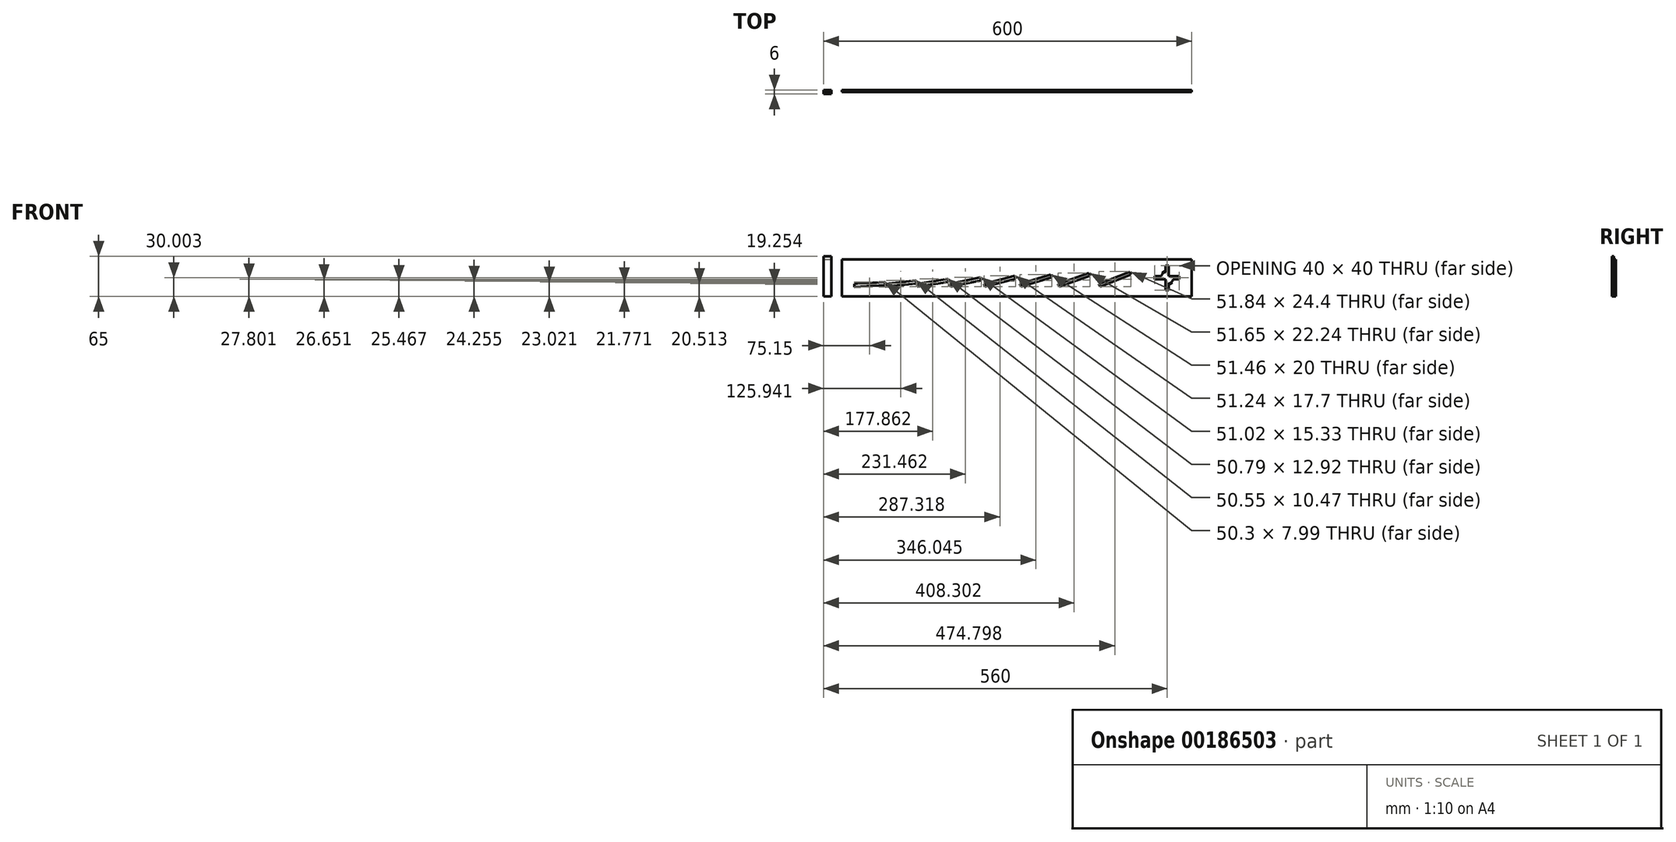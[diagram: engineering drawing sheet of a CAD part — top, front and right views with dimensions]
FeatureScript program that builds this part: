
annotation { "Feature Type Name" : "Feature", "Feature Type Description" : "" }
export const myFeature = defineFeature(function(context is Context, id is Id, definition is map)
    precondition{}
    {
        {
            var Q0;
            Q0=qCreatedBy(makeId("Front.planeOp"),FACE);
            var sketch = newSketch(context, id + "F0", { "sketchPlane" : qUnion([Q0])});
            skLineSegment(sketch, "E0", {"start": v(0, 0) * mm, "end": v(600, 0) * mm, "construction": true});
            skLineSegment(sketch, "E1", {"start": v(0, 0) * mm, "end": v(0, 500) * mm, "construction": true});
            skCircle(sketch, "E2", {"center": v(0, 500) * mm, "radius": 25 * mm, "construction": true});
            skLineSegment(sketch, "E3", {"start": v(0, 500) * mm, "end": v(25, 500) * mm, "construction": true});
            skLineSegment(sketch, "E4", {"start": v(25, 500) * mm, "end": v(600, 500) * mm, "construction": true});
            skLineSegment(sketch, "E5", {"start": v(35, 500) * mm, "end": v(35, 0) * mm, "construction": true});
            skLineSegment(sketch, "E6", {"start": v(35, 0) * mm, "end": v(-24.82, 497.01) * mm, "construction": true});
            skLineSegment(sketch, "E7", {"start": v(85.36, 0) * mm, "end": v(85.36, 3.02) * mm, "construction": true});
            skLineSegment(sketch, "E8", {"start": v(85.36, 0) * mm, "end": v(85, 3) * mm, "construction": true});
            skLineSegment(sketch, "E9", {"start": v(35, 0) * mm, "end": v(85, 3) * mm});
            skLineSegment(sketch, "E10", {"start": v(85, 3) * mm, "end": v(24.82, 502.99) * mm, "construction": true});
            skLineSegment(sketch, "E11", {"start": v(85, 3) * mm, "end": v(85, 3) * mm});
            skLineSegment(sketch, "E12", {"start": v(85, 3) * mm, "end": v(85.36, 3.02) * mm, "construction": true});
            skLineSegment(sketch, "E13", {"start": v(85.67, 0) * mm, "end": v(-24.4, 494.57) * mm, "construction": true});
            skLineSegment(sketch, "E14", {"start": v(136.9, 0) * mm, "end": v(135.67, 5.5) * mm, "construction": true});
            skLineSegment(sketch, "E15", {"start": v(136.9, 0) * mm, "end": v(136.9, 5.63) * mm, "construction": true});
            skLineSegment(sketch, "E16", {"start": v(85.67, 0) * mm, "end": v(135.67, 5.5) * mm});
            skLineSegment(sketch, "E17", {"start": v(135.67, 5.5) * mm, "end": v(24.14, 506.62) * mm, "construction": true});
            skLineSegment(sketch, "E18", {"start": v(135.67, 5.5) * mm, "end": v(136.9, 5.63) * mm, "construction": true});
            skLineSegment(sketch, "E19", {"start": v(137.47, 0) * mm, "end": v(-23.76, 492.22) * mm, "construction": true});
            skLineSegment(sketch, "E20", {"start": v(190.08, 0) * mm, "end": v(190.08, 8.4) * mm, "construction": true});
            skLineSegment(sketch, "E21", {"start": v(137.47, 0) * mm, "end": v(187.47, 7.98) * mm});
            skLineSegment(sketch, "E22", {"start": v(190.08, 0) * mm, "end": v(187.47, 7.98) * mm, "construction": true});
            skLineSegment(sketch, "E23", {"start": v(187.47, 7.98) * mm, "end": v(23.76, 507.78) * mm, "construction": true});
            skLineSegment(sketch, "E24", {"start": v(187.47, 7.98) * mm, "end": v(190.08, 8.4) * mm, "construction": true});
            skLineSegment(sketch, "E25", {"start": v(190.95, 0) * mm, "end": v(-22.91, 490) * mm, "construction": true});
            skLineSegment(sketch, "E26", {"start": v(245.5, 0) * mm, "end": v(240.95, 10.44) * mm, "construction": true});
            skLineSegment(sketch, "E27", {"start": v(245.5, 0) * mm, "end": v(245.5, 11.39) * mm, "construction": true});
            skLineSegment(sketch, "E28", {"start": v(190.95, 0) * mm, "end": v(240.95, 10.44) * mm});
            skLineSegment(sketch, "E29", {"start": v(240.95, 10.44) * mm, "end": v(22.91, 510) * mm, "construction": true});
            skLineSegment(sketch, "E30", {"start": v(240.95, 10.44) * mm, "end": v(245.5, 11.39) * mm, "construction": true});
            skLineSegment(sketch, "E31", {"start": v(246.7, 0) * mm, "end": v(-21.9, 487.94) * mm, "construction": true});
            skLineSegment(sketch, "E32", {"start": v(303.77, 0) * mm, "end": v(303.77, 14.67) * mm, "construction": true});
            skLineSegment(sketch, "E33", {"start": v(246.7, 0) * mm, "end": v(296.7, 12.85) * mm});
            skLineSegment(sketch, "E34", {"start": v(303.77, 0) * mm, "end": v(296.7, 12.85) * mm, "construction": true});
            skLineSegment(sketch, "E35", {"start": v(296.7, 12.85) * mm, "end": v(21.9, 512.06) * mm, "construction": true});
            skLineSegment(sketch, "E36", {"start": v(296.7, 12.85) * mm, "end": v(303.77, 14.67) * mm, "construction": true});
            skLineSegment(sketch, "E37", {"start": v(305.32, 0) * mm, "end": v(-20.76, 486.07) * mm, "construction": true});
            skLineSegment(sketch, "E38", {"start": v(365.53, 0) * mm, "end": v(365.53, 18.32) * mm, "construction": true});
            skLineSegment(sketch, "E39", {"start": v(305.32, 0) * mm, "end": v(355.32, 15.22) * mm});
            skLineSegment(sketch, "E40", {"start": v(365.53, 0) * mm, "end": v(355.32, 15.22) * mm, "construction": true});
            skLineSegment(sketch, "E41", {"start": v(355.32, 15.22) * mm, "end": v(20.76, 513.93) * mm, "construction": true});
            skLineSegment(sketch, "E42", {"start": v(355.32, 15.22) * mm, "end": v(365.53, 18.32) * mm, "construction": true});
            skLineSegment(sketch, "E43", {"start": v(431.47, 0) * mm, "end": v(431.47, 22.43) * mm, "construction": true});
            skLineSegment(sketch, "E44", {"start": v(367.48, 0) * mm, "end": v(-19.53, 484.4) * mm, "construction": true});
            skLineSegment(sketch, "E45", {"start": v(431.47, 0) * mm, "end": v(417.48, 17.52) * mm, "construction": true});
            skLineSegment(sketch, "E46", {"start": v(367.48, 0) * mm, "end": v(417.48, 17.52) * mm});
            skLineSegment(sketch, "E47", {"start": v(417.48, 17.52) * mm, "end": v(19.53, 515.6) * mm, "construction": true});
            skLineSegment(sketch, "E48", {"start": v(417.48, 17.52) * mm, "end": v(431.47, 22.43) * mm, "construction": true});
            skLineSegment(sketch, "E49", {"start": v(433.88, 0) * mm, "end": v(-18.25, 482.91) * mm, "construction": true});
            skLineSegment(sketch, "E50", {"start": v(502.37, 0) * mm, "end": v(502.37, 27.06) * mm, "construction": true});
            skLineSegment(sketch, "E51", {"start": v(502.37, 0) * mm, "end": v(483.88, 19.75) * mm, "construction": true});
            skLineSegment(sketch, "E52", {"start": v(433.88, 0) * mm, "end": v(483.88, 19.75) * mm});
            skLineSegment(sketch, "E53", {"start": v(483.88, 19.75) * mm, "end": v(18.25, 517.09) * mm, "construction": true});
            skLineSegment(sketch, "E54", {"start": v(483.88, 19.75) * mm, "end": v(502.37, 27.06) * mm, "construction": true});
            skLineSegment(sketch, "E55.bottom", {"start": v(-15, -20.25) * mm, "end": v(585, -20.25) * mm});
            skLineSegment(sketch, "E55.top", {"start": v(-15, 39.75) * mm, "end": v(585, 39.75) * mm});
            skLineSegment(sketch, "E55.left", {"start": v(-15, -20.25) * mm, "end": v(-15, 39.75) * mm});
            skLineSegment(sketch, "E55.right", {"start": v(585, -20.25) * mm, "end": v(585, 39.75) * mm});
            skLineSegment(sketch, "E56", {"start": v(35, 0) * mm, "end": v(35.3, -5) * mm});
            skLineSegment(sketch, "E57", {"start": v(35.3, -5) * mm, "end": v(85.3, -2) * mm});
            skLineSegment(sketch, "E58", {"start": v(85, 3) * mm, "end": v(85.3, -2) * mm});
            skLineSegment(sketch, "E59", {"start": v(85.67, 0) * mm, "end": v(86.21, -4.97) * mm});
            skLineSegment(sketch, "E60", {"start": v(86.21, -4.97) * mm, "end": v(136.21, 0.53) * mm});
            skLineSegment(sketch, "E61", {"start": v(135.67, 5.5) * mm, "end": v(136.21, 0.53) * mm});
            skLineSegment(sketch, "E62", {"start": v(137.47, 0) * mm, "end": v(138.26, -4.94) * mm});
            skLineSegment(sketch, "E63", {"start": v(138.26, -4.94) * mm, "end": v(188.26, 3.04) * mm});
            skLineSegment(sketch, "E64", {"start": v(187.47, 7.98) * mm, "end": v(188.26, 3.04) * mm});
            skLineSegment(sketch, "E65", {"start": v(190.95, 0) * mm, "end": v(191.97, -4.9) * mm});
            skLineSegment(sketch, "E66", {"start": v(191.97, -4.9) * mm, "end": v(241.97, 5.54) * mm});
            skLineSegment(sketch, "E67", {"start": v(240.95, 10.44) * mm, "end": v(241.97, 5.54) * mm});
            skLineSegment(sketch, "E68", {"start": v(246.7, 0) * mm, "end": v(247.94, -4.84) * mm});
            skLineSegment(sketch, "E69", {"start": v(296.7, 12.85) * mm, "end": v(297.94, 8) * mm});
            skLineSegment(sketch, "E70", {"start": v(297.94, 8) * mm, "end": v(247.94, -4.84) * mm});
            skLineSegment(sketch, "E71", {"start": v(305.32, 0) * mm, "end": v(306.77, -4.78) * mm});
            skLineSegment(sketch, "E72", {"start": v(306.77, -4.78) * mm, "end": v(356.77, 10.43) * mm});
            skLineSegment(sketch, "E73", {"start": v(355.32, 15.22) * mm, "end": v(356.77, 10.43) * mm});
            skLineSegment(sketch, "E74", {"start": v(367.48, 0) * mm, "end": v(369.13, -4.72) * mm});
            skLineSegment(sketch, "E75", {"start": v(369.13, -4.72) * mm, "end": v(419.13, 12.8) * mm});
            skLineSegment(sketch, "E76", {"start": v(417.48, 17.52) * mm, "end": v(419.13, 12.8) * mm});
            skLineSegment(sketch, "E77", {"start": v(433.88, 0) * mm, "end": v(435.72, -4.65) * mm});
            skLineSegment(sketch, "E78", {"start": v(435.72, -4.65) * mm, "end": v(485.72, 15.1) * mm});
            skLineSegment(sketch, "E79", {"start": v(483.88, 19.75) * mm, "end": v(485.72, 15.1) * mm});
            skLineSegment(sketch, "E80", {"start": v(285, -20.25) * mm, "end": v(285, 39.75) * mm, "construction": true});
            skLineSegment(sketch, "E81.MirrorCS", {"start": v(15, -20.25) * mm, "end": v(15, 39.75) * mm});
            skLineSegment(sketch, "E82", {"start": v(-15, 39.75) * mm, "end": v(-15, 480) * mm});
            skLineSegment(sketch, "E83.MirrorCS", {"start": v(15, 39.75) * mm, "end": v(15, 480) * mm});
            skArc(sketch, "E84", {"start": v(15, 480) * mm, "mid": v(0, 525) * mm, "end": v(-15, 480) * mm});
            skCircle(sketch, "E85", {"center": v(0, 500) * mm, "radius": 5 * mm});
            skCircle(sketch, "E86", {"center": v(10, 490) * mm, "radius": 5 * mm});
            skCircle(sketch, "E87.MirrorC", {"center": v(-10, 490) * mm, "radius": 5 * mm});
            skCircle(sketch, "E88", {"center": v(0, 200) * mm, "radius": 5 * mm});
            skLineSegment(sketch, "E89", {"start": v(0, 500) * mm, "end": v(0, 525) * mm, "construction": true});
            skLineSegment(sketch, "E90", {"start": v(585, 9.75) * mm, "end": v(545, 9.75) * mm, "construction": true});
            skPoint(sketch, "E91", {"position": v(565, 9.75) * mm});
            skLineSegment(sketch, "E92.bottom", {"start": v(565, 12.25) * mm, "end": v(547.5, 12.25) * mm});
            skLineSegment(sketch, "E92.top", {"start": v(565, 7.25) * mm, "end": v(554.68, 7.25) * mm});
            skLineSegment(sketch, "E92.left", {"start": v(565, 12.25) * mm, "end": v(565, 7.25) * mm});
            skLineSegment(sketch, "E92.right", {"start": v(525, 12.25) * mm, "end": v(525, 7.25) * mm});
            skPoint(sketch, "E92.middle", {"position": v(545, 9.75) * mm});
            skLineSegment(sketch, "E93.bottom", {"start": v(547.5, 29.75) * mm, "end": v(542.5, 29.75) * mm});
            skLineSegment(sketch, "E93.top", {"start": v(547.5, -10.25) * mm, "end": v(542.5, -10.25) * mm});
            skLineSegment(sketch, "E93.left", {"start": v(547.5, 29.75) * mm, "end": v(547.5, 12.25) * mm});
            skLineSegment(sketch, "E93.right", {"start": v(542.5, 29.75) * mm, "end": v(542.5, 20.98) * mm});
            skArc(sketch, "E94", {"start": v(535.32, 12.25) * mm, "mid": v(537.75, 16.65) * mm, "end": v(542.02, 19.3) * mm});
            skArc(sketch, "E95", {"start": v(541.55, 19.14) * mm, "mid": v(542.17, 18.82) * mm, "end": v(542.5, 19.44) * mm});
            skLineSegment(sketch, "E96.trimOffspring", {"start": v(535.32, 12.25) * mm, "end": v(525, 12.25) * mm});
            skLineSegment(sketch, "E97.trimOffspring", {"start": v(542.5, 7.25) * mm, "end": v(542.5, -10.25) * mm});
            skLineSegment(sketch, "E98.trimOffspring", {"start": v(542.5, 7.25) * mm, "end": v(525, 7.25) * mm});
            skLineSegment(sketch, "E99.trimOffspring", {"start": v(547.5, 0.07) * mm, "end": v(547.5, -0.96) * mm});
            skArc(sketch, "E100", {"start": v(537.22, 17.53) * mm, "mid": v(539.66, 19.37) * mm, "end": v(542.5, 20.47) * mm});
            skArc(sketch, "E101", {"start": v(536.87, 17.88) * mm, "mid": v(539.46, 19.83) * mm, "end": v(542.5, 20.98) * mm});
            skLineSegment(sketch, "E102.trimOffspring", {"start": v(542.5, 20.47) * mm, "end": v(542.5, 19.16) * mm});
            skLineSegment(sketch, "E103", {"start": v(537.22, 17.53) * mm, "end": v(536.87, 17.88) * mm});
            skLineSegment(sketch, "E104", {"start": v(545, 9.75) * mm, "end": v(545, 4.8) * mm, "construction": true});
            skArc(sketch, "E105.MirrorCS", {"start": v(548.45, 0.37) * mm, "mid": v(547.83, 0.69) * mm, "end": v(547.5, 0.07) * mm});
            skArc(sketch, "E106.MirrorCS", {"start": v(554.68, 7.25) * mm, "mid": v(552.25, 2.86) * mm, "end": v(547.98, 0.2) * mm});
            skArc(sketch, "E107.MirrorCS", {"start": v(552.78, 1.98) * mm, "mid": v(550.34, 0.14) * mm, "end": v(547.5, -0.96) * mm});
            skArc(sketch, "E108.MirrorCS", {"start": v(553.13, 1.62) * mm, "mid": v(550.54, -0.33) * mm, "end": v(547.5, -1.47) * mm});
            skLineSegment(sketch, "E109.MirrorCS", {"start": v(552.78, 1.98) * mm, "end": v(553.13, 1.62) * mm});
            skLineSegment(sketch, "E110.trimOffspring", {"start": v(547.5, -1.47) * mm, "end": v(547.5, -10.25) * mm});
            skLineSegment(sketch, "E111", {"start": v(-15, -20.25) * mm, "end": v(-15, -25.25) * mm});
            skLineSegment(sketch, "E112", {"start": v(-15, -25.25) * mm, "end": v(-2.5, -25.25) * mm});
            skArc(sketch, "E113", {"start": v(-2.5, -25.25) * mm, "mid": v(0, -22.82) * mm, "end": v(-2.35, -20.25) * mm});
            skArc(sketch, "E114.MirrorCS", {"start": v(2.5, -25.25) * mm, "mid": v(0, -22.82) * mm, "end": v(2.35, -20.25) * mm});
            skLineSegment(sketch, "E115.MirrorCS", {"start": v(15, -25.25) * mm, "end": v(2.5, -25.25) * mm});
            skLineSegment(sketch, "E116.MirrorCS", {"start": v(15, -20.25) * mm, "end": v(15, -25.25) * mm});
            skLineSegment(sketch, "E117.bottom", {"start": v(2.35, -20.25) * mm, "end": v(-2.35, -20.25) * mm});
            skLineSegment(sketch, "E117.top", {"start": v(2.35, 39.75) * mm, "end": v(-2.35, 39.75) * mm});
            skLineSegment(sketch, "E117.left", {"start": v(2.35, -20.25) * mm, "end": v(2.35, 39.75) * mm});
            skLineSegment(sketch, "E117.right", {"start": v(-2.35, -20.25) * mm, "end": v(-2.35, 39.75) * mm});
            skLineSegment(sketch, "E118", {"start": v(-2.35, 9.75) * mm, "end": v(2.35, 9.75) * mm});
            skArc(sketch, "E119.MirrorCS", {"start": v(-2.5, 44.75) * mm, "mid": v(0, 42.33) * mm, "end": v(-2.35, 39.75) * mm});
            skArc(sketch, "E120.MirrorCS", {"start": v(2.5, 44.75) * mm, "mid": v(0, 42.33) * mm, "end": v(2.35, 39.75) * mm});
            skLineSegment(sketch, "E121.MirrorCS", {"start": v(15, 44.75) * mm, "end": v(2.5, 44.75) * mm});
            skLineSegment(sketch, "E122.MirrorCS", {"start": v(15, 39.75) * mm, "end": v(15, 44.75) * mm});
            skLineSegment(sketch, "E123.MirrorCS", {"start": v(-15, 44.75) * mm, "end": v(-2.5, 44.75) * mm});
            skLineSegment(sketch, "E124.MirrorCS", {"start": v(-15, 39.75) * mm, "end": v(-15, 44.75) * mm});
            skLineSegment(sketch, "E125.bottom", {"start": v(-2.35, 39.75) * mm, "end": v(2.5, 39.75) * mm});
            skLineSegment(sketch, "E125.top", {"start": v(-2.35, 44.75) * mm, "end": v(2.5, 44.75) * mm});
            skLineSegment(sketch, "E125.left", {"start": v(-2.35, 39.75) * mm, "end": v(-2.35, 44.75) * mm});
            skLineSegment(sketch, "E125.right", {"start": v(2.5, 39.75) * mm, "end": v(2.5, 44.75) * mm});
            skLineSegment(sketch, "E126", {"start": v(32.81, -103.14) * mm, "end": v(82.9, -103.14) * mm, "construction": true});
            skLineSegment(sketch, "E127", {"start": v(82.9, -103.14) * mm, "end": v(38.81, -103.14) * mm});
            skLineSegment(sketch, "E128", {"start": v(37.81, -103.14) * mm, "end": v(32.81, -103.14) * mm});
            skLineSegment(sketch, "E129", {"start": v(38.81, -103.14) * mm, "end": v(38.81, -118.14) * mm});
            skLineSegment(sketch, "E130", {"start": v(38.81, -118.14) * mm, "end": v(37.81, -103.14) * mm});
            skArc(sketch, "E131", {"start": v(32.81, -103.14) * mm, "mid": v(31.81, -104.14) * mm, "end": v(32.81, -105.14) * mm});
            skLineSegment(sketch, "E132", {"start": v(32.81, -105.14) * mm, "end": v(32.81, -110.14) * mm});
            skArc(sketch, "E133", {"start": v(32.81, -110.14) * mm, "mid": v(31.81, -111.14) * mm, "end": v(32.81, -112.14) * mm});
            skLineSegment(sketch, "E134", {"start": v(32.81, -103.14) * mm, "end": v(32.81, -353.14) * mm, "construction": true});
            skLineSegment(sketch, "E135", {"start": v(32.81, -112.14) * mm, "end": v(32.81, -228.14) * mm});
            skLineSegment(sketch, "E136", {"start": v(32.81, -228.14) * mm, "end": v(82.9, -228.14) * mm, "construction": true});
            skLineSegment(sketch, "E137", {"start": v(57.86, -228.14) * mm, "end": v(57.86, -201.59) * mm, "construction": true});
            skArc(sketch, "E138.MirrorCS", {"start": v(82.9, -103.14) * mm, "mid": v(83.9, -104.14) * mm, "end": v(82.9, -105.14) * mm});
            skLineSegment(sketch, "E139.MirrorCS", {"start": v(77.9, -103.14) * mm, "end": v(82.9, -103.14) * mm});
            skLineSegment(sketch, "E140.MirrorCS", {"start": v(82.9, -105.14) * mm, "end": v(82.9, -110.14) * mm});
            skArc(sketch, "E141.MirrorCS", {"start": v(82.9, -110.14) * mm, "mid": v(83.9, -111.14) * mm, "end": v(82.9, -112.14) * mm});
            skLineSegment(sketch, "E142.MirrorCS", {"start": v(76.9, -103.14) * mm, "end": v(76.9, -118.14) * mm});
            skLineSegment(sketch, "E143.MirrorCS", {"start": v(82.9, -112.14) * mm, "end": v(82.9, -228.14) * mm});
            skLineSegment(sketch, "E144.MirrorCS", {"start": v(76.9, -118.14) * mm, "end": v(77.9, -103.14) * mm});
            skArc(sketch, "E145.MirrorCS", {"start": v(32.81, -353.14) * mm, "mid": v(31.81, -352.14) * mm, "end": v(32.81, -351.14) * mm});
            skLineSegment(sketch, "E146.MirrorCS", {"start": v(37.81, -353.14) * mm, "end": v(32.81, -353.14) * mm});
            skArc(sketch, "E147.MirrorCS", {"start": v(82.9, -353.14) * mm, "mid": v(83.9, -352.14) * mm, "end": v(82.9, -351.14) * mm});
            skLineSegment(sketch, "E148.MirrorCS", {"start": v(77.9, -353.14) * mm, "end": v(82.9, -353.14) * mm});
            skArc(sketch, "E149.MirrorCS", {"start": v(32.81, -346.14) * mm, "mid": v(31.81, -345.14) * mm, "end": v(32.81, -344.14) * mm});
            skLineSegment(sketch, "E150.MirrorCS", {"start": v(82.9, -351.14) * mm, "end": v(82.9, -346.14) * mm});
            skArc(sketch, "E151.MirrorCS", {"start": v(82.9, -346.14) * mm, "mid": v(83.9, -345.14) * mm, "end": v(82.9, -344.14) * mm});
            skLineSegment(sketch, "E152.MirrorCS", {"start": v(32.81, -351.14) * mm, "end": v(32.81, -346.14) * mm});
            skLineSegment(sketch, "E153.MirrorCS", {"start": v(38.81, -353.14) * mm, "end": v(38.81, -338.14) * mm});
            skLineSegment(sketch, "E154.MirrorCS", {"start": v(32.81, -344.14) * mm, "end": v(32.81, -228.14) * mm});
            skLineSegment(sketch, "E155.MirrorCS", {"start": v(82.9, -353.14) * mm, "end": v(38.81, -353.14) * mm});
            skLineSegment(sketch, "E156.MirrorCS", {"start": v(82.9, -344.14) * mm, "end": v(82.9, -228.14) * mm});
            skLineSegment(sketch, "E157.MirrorCS", {"start": v(76.9, -353.14) * mm, "end": v(76.9, -338.14) * mm});
            skLineSegment(sketch, "E158.MirrorCS", {"start": v(38.81, -338.14) * mm, "end": v(37.81, -353.14) * mm});
            skLineSegment(sketch, "E159.MirrorCS", {"start": v(32.81, -353.14) * mm, "end": v(82.9, -353.14) * mm, "construction": true});
            skLineSegment(sketch, "E160.MirrorCS", {"start": v(76.9, -338.14) * mm, "end": v(77.9, -353.14) * mm});
            skLineSegment(sketch, "E161.1.0.0", {"start": v(146.9, -123.14) * mm, "end": v(147.9, -103.14) * mm});
            skLineSegment(sketch, "E161.1.0.1", {"start": v(108.81, -123.14) * mm, "end": v(107.81, -103.14) * mm});
            skLineSegment(sketch, "E161.1.0.2", {"start": v(102.81, -103.14) * mm, "end": v(102.81, -353.14) * mm, "construction": true});
            skLineSegment(sketch, "E161.1.0.3", {"start": v(152.9, -112.14) * mm, "end": v(152.9, -228.14) * mm});
            skLineSegment(sketch, "E161.1.0.4", {"start": v(102.81, -228.14) * mm, "end": v(152.9, -228.14) * mm, "construction": true});
            skLineSegment(sketch, "E161.1.0.5", {"start": v(127.86, -228.14) * mm, "end": v(127.86, -201.59) * mm, "construction": true});
            skLineSegment(sketch, "E161.1.0.6", {"start": v(152.9, -344.14) * mm, "end": v(152.9, -228.14) * mm});
            skLineSegment(sketch, "E161.1.0.7", {"start": v(146.9, -333.14) * mm, "end": v(147.9, -353.14) * mm});
            skLineSegment(sketch, "E161.1.0.8", {"start": v(108.81, -333.14) * mm, "end": v(107.81, -353.14) * mm});
            skLineSegment(sketch, "E161.1.0.9", {"start": v(102.81, -103.14) * mm, "end": v(152.9, -103.14) * mm, "construction": true});
            skLineSegment(sketch, "E161.1.0.10", {"start": v(102.81, -353.14) * mm, "end": v(152.9, -353.14) * mm, "construction": true});
            skLineSegment(sketch, "E161.1.0.11", {"start": v(108.81, -103.14) * mm, "end": v(108.81, -123.14) * mm});
            skLineSegment(sketch, "E161.1.0.12", {"start": v(152.9, -353.14) * mm, "end": v(108.81, -353.14) * mm});
            skLineSegment(sketch, "E161.1.0.13", {"start": v(102.81, -344.14) * mm, "end": v(102.81, -228.14) * mm});
            skLineSegment(sketch, "E161.1.0.14", {"start": v(152.9, -103.14) * mm, "end": v(108.81, -103.14) * mm});
            skLineSegment(sketch, "E161.1.0.15", {"start": v(146.9, -353.14) * mm, "end": v(146.9, -333.14) * mm});
            skLineSegment(sketch, "E161.1.0.16", {"start": v(146.9, -103.14) * mm, "end": v(146.9, -123.14) * mm});
            skLineSegment(sketch, "E161.1.0.17", {"start": v(102.81, -112.14) * mm, "end": v(102.81, -228.14) * mm});
            skLineSegment(sketch, "E161.1.0.18", {"start": v(108.81, -353.14) * mm, "end": v(108.81, -333.14) * mm});
            skLineSegment(sketch, "E161.1.0.19", {"start": v(147.9, -103.14) * mm, "end": v(152.9, -103.14) * mm});
            skLineSegment(sketch, "E161.1.0.20", {"start": v(107.81, -103.14) * mm, "end": v(102.81, -103.14) * mm});
            skLineSegment(sketch, "E161.1.0.21", {"start": v(107.81, -353.14) * mm, "end": v(102.81, -353.14) * mm});
            skArc(sketch, "E161.1.0.22", {"start": v(102.81, -346.14) * mm, "mid": v(101.81, -345.14) * mm, "end": v(102.81, -344.14) * mm});
            skLineSegment(sketch, "E161.1.0.23", {"start": v(147.9, -353.14) * mm, "end": v(152.9, -353.14) * mm});
            skArc(sketch, "E161.1.0.24", {"start": v(152.9, -353.14) * mm, "mid": v(153.9, -352.14) * mm, "end": v(152.9, -351.14) * mm});
            skLineSegment(sketch, "E161.1.0.25", {"start": v(102.81, -351.14) * mm, "end": v(102.81, -346.14) * mm});
            skLineSegment(sketch, "E161.1.0.26", {"start": v(152.9, -351.14) * mm, "end": v(152.9, -346.14) * mm});
            skArc(sketch, "E161.1.0.27", {"start": v(152.9, -346.14) * mm, "mid": v(153.9, -345.14) * mm, "end": v(152.9, -344.14) * mm});
            skArc(sketch, "E161.1.0.28", {"start": v(102.81, -353.14) * mm, "mid": v(101.81, -352.14) * mm, "end": v(102.81, -351.14) * mm});
            skArc(sketch, "E161.1.0.29", {"start": v(152.9, -103.14) * mm, "mid": v(153.9, -104.14) * mm, "end": v(152.9, -105.14) * mm});
            skLineSegment(sketch, "E161.1.0.30", {"start": v(152.9, -105.14) * mm, "end": v(152.9, -110.14) * mm});
            skArc(sketch, "E161.1.0.31", {"start": v(152.9, -110.14) * mm, "mid": v(153.9, -111.14) * mm, "end": v(152.9, -112.14) * mm});
            skArc(sketch, "E161.1.0.32", {"start": v(102.81, -103.14) * mm, "mid": v(101.81, -104.14) * mm, "end": v(102.81, -105.14) * mm});
            skLineSegment(sketch, "E161.1.0.33", {"start": v(102.81, -105.14) * mm, "end": v(102.81, -110.14) * mm});
            skArc(sketch, "E161.1.0.34", {"start": v(102.81, -110.14) * mm, "mid": v(101.81, -111.14) * mm, "end": v(102.81, -112.14) * mm});
            skLineSegment(sketch, "E161.2.0.0", {"start": v(216.9, -123.14) * mm, "end": v(217.9, -103.14) * mm});
            skLineSegment(sketch, "E161.2.0.1", {"start": v(178.81, -123.14) * mm, "end": v(177.81, -103.14) * mm});
            skLineSegment(sketch, "E161.2.0.2", {"start": v(172.81, -103.14) * mm, "end": v(172.81, -353.14) * mm, "construction": true});
            skLineSegment(sketch, "E161.2.0.3", {"start": v(222.9, -112.14) * mm, "end": v(222.9, -228.14) * mm});
            skLineSegment(sketch, "E161.2.0.4", {"start": v(172.81, -228.14) * mm, "end": v(222.9, -228.14) * mm, "construction": true});
            skLineSegment(sketch, "E161.2.0.5", {"start": v(197.86, -228.14) * mm, "end": v(197.86, -201.59) * mm, "construction": true});
            skLineSegment(sketch, "E161.2.0.6", {"start": v(222.9, -344.14) * mm, "end": v(222.9, -228.14) * mm});
            skLineSegment(sketch, "E161.2.0.7", {"start": v(216.9, -333.14) * mm, "end": v(217.9, -353.14) * mm});
            skLineSegment(sketch, "E161.2.0.8", {"start": v(178.81, -333.14) * mm, "end": v(177.81, -353.14) * mm});
            skLineSegment(sketch, "E161.2.0.9", {"start": v(172.81, -103.14) * mm, "end": v(222.9, -103.14) * mm, "construction": true});
            skLineSegment(sketch, "E161.2.0.10", {"start": v(172.81, -353.14) * mm, "end": v(222.9, -353.14) * mm, "construction": true});
            skLineSegment(sketch, "E161.2.0.11", {"start": v(178.81, -103.14) * mm, "end": v(178.81, -123.14) * mm});
            skLineSegment(sketch, "E161.2.0.12", {"start": v(222.9, -353.14) * mm, "end": v(178.81, -353.14) * mm});
            skLineSegment(sketch, "E161.2.0.13", {"start": v(172.81, -344.14) * mm, "end": v(172.81, -228.14) * mm});
            skLineSegment(sketch, "E161.2.0.14", {"start": v(222.9, -103.14) * mm, "end": v(178.81, -103.14) * mm});
            skLineSegment(sketch, "E161.2.0.15", {"start": v(216.9, -353.14) * mm, "end": v(216.9, -333.14) * mm});
            skLineSegment(sketch, "E161.2.0.16", {"start": v(216.9, -103.14) * mm, "end": v(216.9, -123.14) * mm});
            skLineSegment(sketch, "E161.2.0.17", {"start": v(172.81, -112.14) * mm, "end": v(172.81, -228.14) * mm});
            skLineSegment(sketch, "E161.2.0.18", {"start": v(178.81, -353.14) * mm, "end": v(178.81, -333.14) * mm});
            skLineSegment(sketch, "E161.2.0.19", {"start": v(217.9, -103.14) * mm, "end": v(222.9, -103.14) * mm});
            skLineSegment(sketch, "E161.2.0.20", {"start": v(177.81, -103.14) * mm, "end": v(172.81, -103.14) * mm});
            skLineSegment(sketch, "E161.2.0.21", {"start": v(177.81, -353.14) * mm, "end": v(172.81, -353.14) * mm});
            skArc(sketch, "E161.2.0.22", {"start": v(172.81, -346.14) * mm, "mid": v(171.81, -345.14) * mm, "end": v(172.81, -344.14) * mm});
            skLineSegment(sketch, "E161.2.0.23", {"start": v(217.9, -353.14) * mm, "end": v(222.9, -353.14) * mm});
            skArc(sketch, "E161.2.0.24", {"start": v(222.9, -353.14) * mm, "mid": v(223.9, -352.14) * mm, "end": v(222.9, -351.14) * mm});
            skLineSegment(sketch, "E161.2.0.25", {"start": v(172.81, -351.14) * mm, "end": v(172.81, -346.14) * mm});
            skLineSegment(sketch, "E161.2.0.26", {"start": v(222.9, -351.14) * mm, "end": v(222.9, -346.14) * mm});
            skArc(sketch, "E161.2.0.27", {"start": v(222.9, -346.14) * mm, "mid": v(223.9, -345.14) * mm, "end": v(222.9, -344.14) * mm});
            skArc(sketch, "E161.2.0.28", {"start": v(172.81, -353.14) * mm, "mid": v(171.81, -352.14) * mm, "end": v(172.81, -351.14) * mm});
            skArc(sketch, "E161.2.0.29", {"start": v(222.9, -103.14) * mm, "mid": v(223.9, -104.14) * mm, "end": v(222.9, -105.14) * mm});
            skLineSegment(sketch, "E161.2.0.30", {"start": v(222.9, -105.14) * mm, "end": v(222.9, -110.14) * mm});
            skArc(sketch, "E161.2.0.31", {"start": v(222.9, -110.14) * mm, "mid": v(223.9, -111.14) * mm, "end": v(222.9, -112.14) * mm});
            skArc(sketch, "E161.2.0.32", {"start": v(172.81, -103.14) * mm, "mid": v(171.81, -104.14) * mm, "end": v(172.81, -105.14) * mm});
            skLineSegment(sketch, "E161.2.0.33", {"start": v(172.81, -105.14) * mm, "end": v(172.81, -110.14) * mm});
            skArc(sketch, "E161.2.0.34", {"start": v(172.81, -110.14) * mm, "mid": v(171.81, -111.14) * mm, "end": v(172.81, -112.14) * mm});
            skLineSegment(sketch, "E161.3.0.0", {"start": v(286.9, -123.14) * mm, "end": v(287.9, -103.14) * mm});
            skLineSegment(sketch, "E161.3.0.1", {"start": v(248.81, -123.14) * mm, "end": v(247.81, -103.14) * mm});
            skLineSegment(sketch, "E161.3.0.2", {"start": v(242.81, -103.14) * mm, "end": v(242.81, -353.14) * mm, "construction": true});
            skLineSegment(sketch, "E161.3.0.3", {"start": v(292.9, -112.14) * mm, "end": v(292.9, -228.14) * mm});
            skLineSegment(sketch, "E161.3.0.4", {"start": v(242.81, -228.14) * mm, "end": v(292.9, -228.14) * mm, "construction": true});
            skLineSegment(sketch, "E161.3.0.5", {"start": v(267.86, -228.14) * mm, "end": v(267.86, -201.59) * mm, "construction": true});
            skLineSegment(sketch, "E161.3.0.6", {"start": v(292.9, -344.14) * mm, "end": v(292.9, -228.14) * mm});
            skLineSegment(sketch, "E161.3.0.7", {"start": v(286.9, -333.14) * mm, "end": v(287.9, -353.14) * mm});
            skLineSegment(sketch, "E161.3.0.8", {"start": v(248.81, -333.14) * mm, "end": v(247.81, -353.14) * mm});
            skLineSegment(sketch, "E161.3.0.9", {"start": v(242.81, -103.14) * mm, "end": v(292.9, -103.14) * mm, "construction": true});
            skLineSegment(sketch, "E161.3.0.10", {"start": v(242.81, -353.14) * mm, "end": v(292.9, -353.14) * mm, "construction": true});
            skLineSegment(sketch, "E161.3.0.11", {"start": v(248.81, -103.14) * mm, "end": v(248.81, -123.14) * mm});
            skLineSegment(sketch, "E161.3.0.12", {"start": v(292.9, -353.14) * mm, "end": v(248.81, -353.14) * mm});
            skLineSegment(sketch, "E161.3.0.13", {"start": v(242.81, -344.14) * mm, "end": v(242.81, -228.14) * mm});
            skLineSegment(sketch, "E161.3.0.14", {"start": v(292.9, -103.14) * mm, "end": v(248.81, -103.14) * mm});
            skLineSegment(sketch, "E161.3.0.15", {"start": v(286.9, -353.14) * mm, "end": v(286.9, -333.14) * mm});
            skLineSegment(sketch, "E161.3.0.16", {"start": v(286.9, -103.14) * mm, "end": v(286.9, -123.14) * mm});
            skLineSegment(sketch, "E161.3.0.17", {"start": v(242.81, -112.14) * mm, "end": v(242.81, -228.14) * mm});
            skLineSegment(sketch, "E161.3.0.18", {"start": v(248.81, -353.14) * mm, "end": v(248.81, -333.14) * mm});
            skLineSegment(sketch, "E161.3.0.19", {"start": v(287.9, -103.14) * mm, "end": v(292.9, -103.14) * mm});
            skLineSegment(sketch, "E161.3.0.20", {"start": v(247.81, -103.14) * mm, "end": v(242.81, -103.14) * mm});
            skLineSegment(sketch, "E161.3.0.21", {"start": v(247.81, -353.14) * mm, "end": v(242.81, -353.14) * mm});
            skArc(sketch, "E161.3.0.22", {"start": v(242.81, -346.14) * mm, "mid": v(241.81, -345.14) * mm, "end": v(242.81, -344.14) * mm});
            skLineSegment(sketch, "E161.3.0.23", {"start": v(287.9, -353.14) * mm, "end": v(292.9, -353.14) * mm});
            skArc(sketch, "E161.3.0.24", {"start": v(292.9, -353.14) * mm, "mid": v(293.9, -352.14) * mm, "end": v(292.9, -351.14) * mm});
            skLineSegment(sketch, "E161.3.0.25", {"start": v(242.81, -351.14) * mm, "end": v(242.81, -346.14) * mm});
            skLineSegment(sketch, "E161.3.0.26", {"start": v(292.9, -351.14) * mm, "end": v(292.9, -346.14) * mm});
            skArc(sketch, "E161.3.0.27", {"start": v(292.9, -346.14) * mm, "mid": v(293.9, -345.14) * mm, "end": v(292.9, -344.14) * mm});
            skArc(sketch, "E161.3.0.28", {"start": v(242.81, -353.14) * mm, "mid": v(241.81, -352.14) * mm, "end": v(242.81, -351.14) * mm});
            skArc(sketch, "E161.3.0.29", {"start": v(292.9, -103.14) * mm, "mid": v(293.9, -104.14) * mm, "end": v(292.9, -105.14) * mm});
            skLineSegment(sketch, "E161.3.0.30", {"start": v(292.9, -105.14) * mm, "end": v(292.9, -110.14) * mm});
            skArc(sketch, "E161.3.0.31", {"start": v(292.9, -110.14) * mm, "mid": v(293.9, -111.14) * mm, "end": v(292.9, -112.14) * mm});
            skArc(sketch, "E161.3.0.32", {"start": v(242.81, -103.14) * mm, "mid": v(241.81, -104.14) * mm, "end": v(242.81, -105.14) * mm});
            skLineSegment(sketch, "E161.3.0.33", {"start": v(242.81, -105.14) * mm, "end": v(242.81, -110.14) * mm});
            skArc(sketch, "E161.3.0.34", {"start": v(242.81, -110.14) * mm, "mid": v(241.81, -111.14) * mm, "end": v(242.81, -112.14) * mm});
            skLineSegment(sketch, "E161.4.0.0", {"start": v(356.9, -123.14) * mm, "end": v(357.9, -103.14) * mm});
            skLineSegment(sketch, "E161.4.0.1", {"start": v(318.81, -123.14) * mm, "end": v(317.81, -103.14) * mm});
            skLineSegment(sketch, "E161.4.0.2", {"start": v(312.81, -103.14) * mm, "end": v(312.81, -353.14) * mm, "construction": true});
            skLineSegment(sketch, "E161.4.0.3", {"start": v(362.9, -112.14) * mm, "end": v(362.9, -228.14) * mm});
            skLineSegment(sketch, "E161.4.0.4", {"start": v(312.81, -228.14) * mm, "end": v(362.9, -228.14) * mm, "construction": true});
            skLineSegment(sketch, "E161.4.0.5", {"start": v(337.86, -228.14) * mm, "end": v(337.86, -201.59) * mm, "construction": true});
            skLineSegment(sketch, "E161.4.0.6", {"start": v(362.9, -344.14) * mm, "end": v(362.9, -228.14) * mm});
            skLineSegment(sketch, "E161.4.0.7", {"start": v(356.9, -333.14) * mm, "end": v(357.9, -353.14) * mm});
            skLineSegment(sketch, "E161.4.0.8", {"start": v(318.81, -333.14) * mm, "end": v(317.81, -353.14) * mm});
            skLineSegment(sketch, "E161.4.0.9", {"start": v(312.81, -103.14) * mm, "end": v(362.9, -103.14) * mm, "construction": true});
            skLineSegment(sketch, "E161.4.0.10", {"start": v(312.81, -353.14) * mm, "end": v(362.9, -353.14) * mm, "construction": true});
            skLineSegment(sketch, "E161.4.0.11", {"start": v(318.81, -103.14) * mm, "end": v(318.81, -123.14) * mm});
            skLineSegment(sketch, "E161.4.0.12", {"start": v(362.9, -353.14) * mm, "end": v(318.81, -353.14) * mm});
            skLineSegment(sketch, "E161.4.0.13", {"start": v(312.81, -344.14) * mm, "end": v(312.81, -228.14) * mm});
            skLineSegment(sketch, "E161.4.0.14", {"start": v(362.9, -103.14) * mm, "end": v(318.81, -103.14) * mm});
            skLineSegment(sketch, "E161.4.0.15", {"start": v(356.9, -353.14) * mm, "end": v(356.9, -333.14) * mm});
            skLineSegment(sketch, "E161.4.0.16", {"start": v(356.9, -103.14) * mm, "end": v(356.9, -123.14) * mm});
            skLineSegment(sketch, "E161.4.0.17", {"start": v(312.81, -112.14) * mm, "end": v(312.81, -228.14) * mm});
            skLineSegment(sketch, "E161.4.0.18", {"start": v(318.81, -353.14) * mm, "end": v(318.81, -333.14) * mm});
            skLineSegment(sketch, "E161.4.0.19", {"start": v(357.9, -103.14) * mm, "end": v(362.9, -103.14) * mm});
            skLineSegment(sketch, "E161.4.0.20", {"start": v(317.81, -103.14) * mm, "end": v(312.81, -103.14) * mm});
            skLineSegment(sketch, "E161.4.0.21", {"start": v(317.81, -353.14) * mm, "end": v(312.81, -353.14) * mm});
            skArc(sketch, "E161.4.0.22", {"start": v(312.81, -346.14) * mm, "mid": v(311.81, -345.14) * mm, "end": v(312.81, -344.14) * mm});
            skLineSegment(sketch, "E161.4.0.23", {"start": v(357.9, -353.14) * mm, "end": v(362.9, -353.14) * mm});
            skArc(sketch, "E161.4.0.24", {"start": v(362.9, -353.14) * mm, "mid": v(363.9, -352.14) * mm, "end": v(362.9, -351.14) * mm});
            skLineSegment(sketch, "E161.4.0.25", {"start": v(312.81, -351.14) * mm, "end": v(312.81, -346.14) * mm});
            skLineSegment(sketch, "E161.4.0.26", {"start": v(362.9, -351.14) * mm, "end": v(362.9, -346.14) * mm});
            skArc(sketch, "E161.4.0.27", {"start": v(362.9, -346.14) * mm, "mid": v(363.9, -345.14) * mm, "end": v(362.9, -344.14) * mm});
            skArc(sketch, "E161.4.0.28", {"start": v(312.81, -353.14) * mm, "mid": v(311.81, -352.14) * mm, "end": v(312.81, -351.14) * mm});
            skArc(sketch, "E161.4.0.29", {"start": v(362.9, -103.14) * mm, "mid": v(363.9, -104.14) * mm, "end": v(362.9, -105.14) * mm});
            skLineSegment(sketch, "E161.4.0.30", {"start": v(362.9, -105.14) * mm, "end": v(362.9, -110.14) * mm});
            skArc(sketch, "E161.4.0.31", {"start": v(362.9, -110.14) * mm, "mid": v(363.9, -111.14) * mm, "end": v(362.9, -112.14) * mm});
            skArc(sketch, "E161.4.0.32", {"start": v(312.81, -103.14) * mm, "mid": v(311.81, -104.14) * mm, "end": v(312.81, -105.14) * mm});
            skLineSegment(sketch, "E161.4.0.33", {"start": v(312.81, -105.14) * mm, "end": v(312.81, -110.14) * mm});
            skArc(sketch, "E161.4.0.34", {"start": v(312.81, -110.14) * mm, "mid": v(311.81, -111.14) * mm, "end": v(312.81, -112.14) * mm});
            skLineSegment(sketch, "E161.5.0.0", {"start": v(426.9, -123.14) * mm, "end": v(427.9, -103.14) * mm});
            skLineSegment(sketch, "E161.5.0.1", {"start": v(388.81, -123.14) * mm, "end": v(387.81, -103.14) * mm});
            skLineSegment(sketch, "E161.5.0.2", {"start": v(382.81, -103.14) * mm, "end": v(382.81, -353.14) * mm, "construction": true});
            skLineSegment(sketch, "E161.5.0.3", {"start": v(432.9, -112.14) * mm, "end": v(432.9, -228.14) * mm});
            skLineSegment(sketch, "E161.5.0.4", {"start": v(382.81, -228.14) * mm, "end": v(432.9, -228.14) * mm, "construction": true});
            skLineSegment(sketch, "E161.5.0.5", {"start": v(407.86, -228.14) * mm, "end": v(407.86, -201.59) * mm, "construction": true});
            skLineSegment(sketch, "E161.5.0.6", {"start": v(432.9, -344.14) * mm, "end": v(432.9, -228.14) * mm});
            skLineSegment(sketch, "E161.5.0.7", {"start": v(426.9, -333.14) * mm, "end": v(427.9, -353.14) * mm});
            skLineSegment(sketch, "E161.5.0.8", {"start": v(388.81, -333.14) * mm, "end": v(387.81, -353.14) * mm});
            skLineSegment(sketch, "E161.5.0.9", {"start": v(382.81, -103.14) * mm, "end": v(432.9, -103.14) * mm, "construction": true});
            skLineSegment(sketch, "E161.5.0.10", {"start": v(382.81, -353.14) * mm, "end": v(432.9, -353.14) * mm, "construction": true});
            skLineSegment(sketch, "E161.5.0.11", {"start": v(388.81, -103.14) * mm, "end": v(388.81, -123.14) * mm});
            skLineSegment(sketch, "E161.5.0.12", {"start": v(432.9, -353.14) * mm, "end": v(388.81, -353.14) * mm});
            skLineSegment(sketch, "E161.5.0.13", {"start": v(382.81, -344.14) * mm, "end": v(382.81, -228.14) * mm});
            skLineSegment(sketch, "E161.5.0.14", {"start": v(432.9, -103.14) * mm, "end": v(388.81, -103.14) * mm});
            skLineSegment(sketch, "E161.5.0.15", {"start": v(426.9, -353.14) * mm, "end": v(426.9, -333.14) * mm});
            skLineSegment(sketch, "E161.5.0.16", {"start": v(426.9, -103.14) * mm, "end": v(426.9, -123.14) * mm});
            skLineSegment(sketch, "E161.5.0.17", {"start": v(382.81, -112.14) * mm, "end": v(382.81, -228.14) * mm});
            skLineSegment(sketch, "E161.5.0.18", {"start": v(388.81, -353.14) * mm, "end": v(388.81, -333.14) * mm});
            skLineSegment(sketch, "E161.5.0.19", {"start": v(427.9, -103.14) * mm, "end": v(432.9, -103.14) * mm});
            skLineSegment(sketch, "E161.5.0.20", {"start": v(387.81, -103.14) * mm, "end": v(382.81, -103.14) * mm});
            skLineSegment(sketch, "E161.5.0.21", {"start": v(387.81, -353.14) * mm, "end": v(382.81, -353.14) * mm});
            skArc(sketch, "E161.5.0.22", {"start": v(382.81, -346.14) * mm, "mid": v(381.81, -345.14) * mm, "end": v(382.81, -344.14) * mm});
            skLineSegment(sketch, "E161.5.0.23", {"start": v(427.9, -353.14) * mm, "end": v(432.9, -353.14) * mm});
            skArc(sketch, "E161.5.0.24", {"start": v(432.9, -353.14) * mm, "mid": v(433.9, -352.14) * mm, "end": v(432.9, -351.14) * mm});
            skLineSegment(sketch, "E161.5.0.25", {"start": v(382.81, -351.14) * mm, "end": v(382.81, -346.14) * mm});
            skLineSegment(sketch, "E161.5.0.26", {"start": v(432.9, -351.14) * mm, "end": v(432.9, -346.14) * mm});
            skArc(sketch, "E161.5.0.27", {"start": v(432.9, -346.14) * mm, "mid": v(433.9, -345.14) * mm, "end": v(432.9, -344.14) * mm});
            skArc(sketch, "E161.5.0.28", {"start": v(382.81, -353.14) * mm, "mid": v(381.81, -352.14) * mm, "end": v(382.81, -351.14) * mm});
            skArc(sketch, "E161.5.0.29", {"start": v(432.9, -103.14) * mm, "mid": v(433.9, -104.14) * mm, "end": v(432.9, -105.14) * mm});
            skLineSegment(sketch, "E161.5.0.30", {"start": v(432.9, -105.14) * mm, "end": v(432.9, -110.14) * mm});
            skArc(sketch, "E161.5.0.31", {"start": v(432.9, -110.14) * mm, "mid": v(433.9, -111.14) * mm, "end": v(432.9, -112.14) * mm});
            skArc(sketch, "E161.5.0.32", {"start": v(382.81, -103.14) * mm, "mid": v(381.81, -104.14) * mm, "end": v(382.81, -105.14) * mm});
            skLineSegment(sketch, "E161.5.0.33", {"start": v(382.81, -105.14) * mm, "end": v(382.81, -110.14) * mm});
            skArc(sketch, "E161.5.0.34", {"start": v(382.81, -110.14) * mm, "mid": v(381.81, -111.14) * mm, "end": v(382.81, -112.14) * mm});
            skLineSegment(sketch, "E161.6.0.0", {"start": v(496.9, -123.14) * mm, "end": v(497.9, -103.14) * mm});
            skLineSegment(sketch, "E161.6.0.1", {"start": v(458.81, -123.14) * mm, "end": v(457.81, -103.14) * mm});
            skLineSegment(sketch, "E161.6.0.2", {"start": v(452.81, -103.14) * mm, "end": v(452.81, -353.14) * mm, "construction": true});
            skLineSegment(sketch, "E161.6.0.3", {"start": v(502.9, -112.14) * mm, "end": v(502.9, -228.14) * mm});
            skLineSegment(sketch, "E161.6.0.4", {"start": v(452.81, -228.14) * mm, "end": v(502.9, -228.14) * mm, "construction": true});
            skLineSegment(sketch, "E161.6.0.5", {"start": v(477.86, -228.14) * mm, "end": v(477.86, -201.59) * mm, "construction": true});
            skLineSegment(sketch, "E161.6.0.6", {"start": v(502.9, -344.14) * mm, "end": v(502.9, -228.14) * mm});
            skLineSegment(sketch, "E161.6.0.7", {"start": v(496.9, -333.14) * mm, "end": v(497.9, -353.14) * mm});
            skLineSegment(sketch, "E161.6.0.8", {"start": v(458.81, -333.14) * mm, "end": v(457.81, -353.14) * mm});
            skLineSegment(sketch, "E161.6.0.9", {"start": v(452.81, -103.14) * mm, "end": v(502.9, -103.14) * mm, "construction": true});
            skLineSegment(sketch, "E161.6.0.10", {"start": v(452.81, -353.14) * mm, "end": v(502.9, -353.14) * mm, "construction": true});
            skLineSegment(sketch, "E161.6.0.11", {"start": v(458.81, -103.14) * mm, "end": v(458.81, -123.14) * mm});
            skLineSegment(sketch, "E161.6.0.12", {"start": v(502.9, -353.14) * mm, "end": v(458.81, -353.14) * mm});
            skLineSegment(sketch, "E161.6.0.13", {"start": v(452.81, -344.14) * mm, "end": v(452.81, -228.14) * mm});
            skLineSegment(sketch, "E161.6.0.14", {"start": v(502.9, -103.14) * mm, "end": v(458.81, -103.14) * mm});
            skLineSegment(sketch, "E161.6.0.15", {"start": v(496.9, -353.14) * mm, "end": v(496.9, -333.14) * mm});
            skLineSegment(sketch, "E161.6.0.16", {"start": v(496.9, -103.14) * mm, "end": v(496.9, -123.14) * mm});
            skLineSegment(sketch, "E161.6.0.17", {"start": v(452.81, -112.14) * mm, "end": v(452.81, -228.14) * mm});
            skLineSegment(sketch, "E161.6.0.18", {"start": v(458.81, -353.14) * mm, "end": v(458.81, -333.14) * mm});
            skLineSegment(sketch, "E161.6.0.19", {"start": v(497.9, -103.14) * mm, "end": v(502.9, -103.14) * mm});
            skLineSegment(sketch, "E161.6.0.20", {"start": v(457.81, -103.14) * mm, "end": v(452.81, -103.14) * mm});
            skLineSegment(sketch, "E161.6.0.21", {"start": v(457.81, -353.14) * mm, "end": v(452.81, -353.14) * mm});
            skArc(sketch, "E161.6.0.22", {"start": v(452.81, -346.14) * mm, "mid": v(451.81, -345.14) * mm, "end": v(452.81, -344.14) * mm});
            skLineSegment(sketch, "E161.6.0.23", {"start": v(497.9, -353.14) * mm, "end": v(502.9, -353.14) * mm});
            skArc(sketch, "E161.6.0.24", {"start": v(502.9, -353.14) * mm, "mid": v(503.9, -352.14) * mm, "end": v(502.9, -351.14) * mm});
            skLineSegment(sketch, "E161.6.0.25", {"start": v(452.81, -351.14) * mm, "end": v(452.81, -346.14) * mm});
            skLineSegment(sketch, "E161.6.0.26", {"start": v(502.9, -351.14) * mm, "end": v(502.9, -346.14) * mm});
            skArc(sketch, "E161.6.0.27", {"start": v(502.9, -346.14) * mm, "mid": v(503.9, -345.14) * mm, "end": v(502.9, -344.14) * mm});
            skArc(sketch, "E161.6.0.28", {"start": v(452.81, -353.14) * mm, "mid": v(451.81, -352.14) * mm, "end": v(452.81, -351.14) * mm});
            skArc(sketch, "E161.6.0.29", {"start": v(502.9, -103.14) * mm, "mid": v(503.9, -104.14) * mm, "end": v(502.9, -105.14) * mm});
            skLineSegment(sketch, "E161.6.0.30", {"start": v(502.9, -105.14) * mm, "end": v(502.9, -110.14) * mm});
            skArc(sketch, "E161.6.0.31", {"start": v(502.9, -110.14) * mm, "mid": v(503.9, -111.14) * mm, "end": v(502.9, -112.14) * mm});
            skArc(sketch, "E161.6.0.32", {"start": v(452.81, -103.14) * mm, "mid": v(451.81, -104.14) * mm, "end": v(452.81, -105.14) * mm});
            skLineSegment(sketch, "E161.6.0.33", {"start": v(452.81, -105.14) * mm, "end": v(452.81, -110.14) * mm});
            skArc(sketch, "E161.6.0.34", {"start": v(452.81, -110.14) * mm, "mid": v(451.81, -111.14) * mm, "end": v(452.81, -112.14) * mm});
            skLineSegment(sketch, "E161.7.0.0", {"start": v(566.9, -123.14) * mm, "end": v(567.9, -103.14) * mm});
            skLineSegment(sketch, "E161.7.0.1", {"start": v(528.81, -123.14) * mm, "end": v(527.81, -103.14) * mm});
            skLineSegment(sketch, "E161.7.0.2", {"start": v(522.81, -103.14) * mm, "end": v(522.81, -353.14) * mm, "construction": true});
            skLineSegment(sketch, "E161.7.0.3", {"start": v(572.9, -112.14) * mm, "end": v(572.9, -228.14) * mm});
            skLineSegment(sketch, "E161.7.0.4", {"start": v(522.81, -228.14) * mm, "end": v(572.9, -228.14) * mm, "construction": true});
            skLineSegment(sketch, "E161.7.0.5", {"start": v(547.86, -228.14) * mm, "end": v(547.86, -201.59) * mm, "construction": true});
            skLineSegment(sketch, "E161.7.0.6", {"start": v(572.9, -344.14) * mm, "end": v(572.9, -228.14) * mm});
            skLineSegment(sketch, "E161.7.0.7", {"start": v(566.9, -333.14) * mm, "end": v(567.9, -353.14) * mm});
            skLineSegment(sketch, "E161.7.0.8", {"start": v(528.81, -333.14) * mm, "end": v(527.81, -353.14) * mm});
            skLineSegment(sketch, "E161.7.0.9", {"start": v(522.81, -103.14) * mm, "end": v(572.9, -103.14) * mm, "construction": true});
            skLineSegment(sketch, "E161.7.0.10", {"start": v(522.81, -353.14) * mm, "end": v(572.9, -353.14) * mm, "construction": true});
            skLineSegment(sketch, "E161.7.0.11", {"start": v(528.81, -103.14) * mm, "end": v(528.81, -123.14) * mm});
            skLineSegment(sketch, "E161.7.0.12", {"start": v(572.9, -353.14) * mm, "end": v(528.81, -353.14) * mm});
            skLineSegment(sketch, "E161.7.0.13", {"start": v(522.81, -344.14) * mm, "end": v(522.81, -228.14) * mm});
            skLineSegment(sketch, "E161.7.0.14", {"start": v(572.9, -103.14) * mm, "end": v(528.81, -103.14) * mm});
            skLineSegment(sketch, "E161.7.0.15", {"start": v(566.9, -353.14) * mm, "end": v(566.9, -333.14) * mm});
            skLineSegment(sketch, "E161.7.0.16", {"start": v(566.9, -103.14) * mm, "end": v(566.9, -123.14) * mm});
            skLineSegment(sketch, "E161.7.0.17", {"start": v(522.81, -112.14) * mm, "end": v(522.81, -228.14) * mm});
            skLineSegment(sketch, "E161.7.0.18", {"start": v(528.81, -353.14) * mm, "end": v(528.81, -333.14) * mm});
            skLineSegment(sketch, "E161.7.0.19", {"start": v(567.9, -103.14) * mm, "end": v(572.9, -103.14) * mm});
            skLineSegment(sketch, "E161.7.0.20", {"start": v(527.81, -103.14) * mm, "end": v(522.81, -103.14) * mm});
            skLineSegment(sketch, "E161.7.0.21", {"start": v(527.81, -353.14) * mm, "end": v(522.81, -353.14) * mm});
            skArc(sketch, "E161.7.0.22", {"start": v(522.81, -346.14) * mm, "mid": v(521.81, -345.14) * mm, "end": v(522.81, -344.14) * mm});
            skLineSegment(sketch, "E161.7.0.23", {"start": v(567.9, -353.14) * mm, "end": v(572.9, -353.14) * mm});
            skArc(sketch, "E161.7.0.24", {"start": v(572.9, -353.14) * mm, "mid": v(573.9, -352.14) * mm, "end": v(572.9, -351.14) * mm});
            skLineSegment(sketch, "E161.7.0.25", {"start": v(522.81, -351.14) * mm, "end": v(522.81, -346.14) * mm});
            skLineSegment(sketch, "E161.7.0.26", {"start": v(572.9, -351.14) * mm, "end": v(572.9, -346.14) * mm});
            skArc(sketch, "E161.7.0.27", {"start": v(572.9, -346.14) * mm, "mid": v(573.9, -345.14) * mm, "end": v(572.9, -344.14) * mm});
            skArc(sketch, "E161.7.0.28", {"start": v(522.81, -353.14) * mm, "mid": v(521.81, -352.14) * mm, "end": v(522.81, -351.14) * mm});
            skArc(sketch, "E161.7.0.29", {"start": v(572.9, -103.14) * mm, "mid": v(573.9, -104.14) * mm, "end": v(572.9, -105.14) * mm});
            skLineSegment(sketch, "E161.7.0.30", {"start": v(572.9, -105.14) * mm, "end": v(572.9, -110.14) * mm});
            skArc(sketch, "E161.7.0.31", {"start": v(572.9, -110.14) * mm, "mid": v(573.9, -111.14) * mm, "end": v(572.9, -112.14) * mm});
            skArc(sketch, "E161.7.0.32", {"start": v(522.81, -103.14) * mm, "mid": v(521.81, -104.14) * mm, "end": v(522.81, -105.14) * mm});
            skLineSegment(sketch, "E161.7.0.33", {"start": v(522.81, -105.14) * mm, "end": v(522.81, -110.14) * mm});
            skArc(sketch, "E161.7.0.34", {"start": v(522.81, -110.14) * mm, "mid": v(521.81, -111.14) * mm, "end": v(522.81, -112.14) * mm});
            skLineSegment(sketch, "E161.direction1", {"start": v(32.81, -353.14) * mm, "end": v(102.81, -353.14) * mm, "construction": true});
            skSolve(sketch);
        }
        {
            var Q0;
            {var subQ1=sQuery(id+"F0.wireOp",EDGE,"E55.left");Q0=makeQuery(id+"F0.imprint","IMPRINT",FACE,{"disambiguationData":[TD([[makeQuery(id+"F0.imprint","IMPRINT",EDGE,{"derivedFrom":subQ1}),-1.0]])]});}
            var Q1;
            {var subQ1=sQuery(id+"F0.wireOp",EDGE,"E82");Q1=makeQuery(id+"F0.imprint","IMPRINT",FACE,{"disambiguationData":[TD([[makeQuery(id+"F0.imprint","IMPRINT",EDGE,{"derivedFrom":subQ1}),-1.0]])]});}
            extrude(context, id + "F1", {"entities" : qUnion([Q0, Q1]), "depth" : 3 * mm});
        }
        {
            var Q0;
            Q0=makeQuery(id+"F0.imprint","IMPRINT",FACE,{"disambiguationData":[TD([[makeQuery(id+"F0.imprint","IMPRINT",EDGE,{"derivedFrom":sQuery(id+"F0.wireOp",EDGE,"E9")}),1.0]])]});
            var Q1;
            {var subQ1=sQuery(id+"F0.wireOp",EDGE,"E55.left");Q1=makeQuery(id+"F0.imprint","IMPRINT",FACE,{"disambiguationData":[TD([[makeQuery(id+"F0.imprint","IMPRINT",EDGE,{"derivedFrom":subQ1}),-1.0]])]});}
            extrude(context, id + "F2", {"entities" : qUnion([Q0, Q1]), "oppositeDirection" : true, "depth" : 3 * mm});
        }
    });
